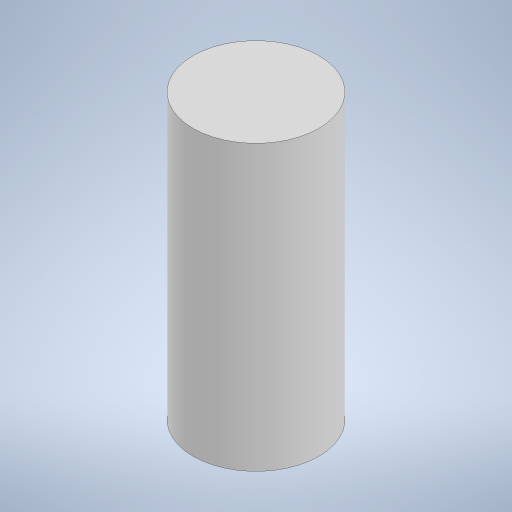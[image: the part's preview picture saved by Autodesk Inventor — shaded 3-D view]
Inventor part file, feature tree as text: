
AUTODESK INVENTOR PART (.ipt)
format: ipt  version: 2024 (Build 280153000, 153)  size: 201,728 bytes
history: native  units: in
note: dims shown in document units (in); Inventor stores cm internally (conversion verified against a paired STEP export)
features: extrude x1, sketch x1
ambient origin geometry x8: Origin, YZ Plane, XZ Plane, XY Plane, X Axis, Y Axis, Z Axis, Center Point
bodies: Solid1 (feature_tree)
feature tree (2):
  extrude  "Extrusion1"  Depth=4.0in TaperAngle=0.0deg
  sketch  "Sketch1"  dims[d0=1.772in d1=4.0in d2=0.0in]
